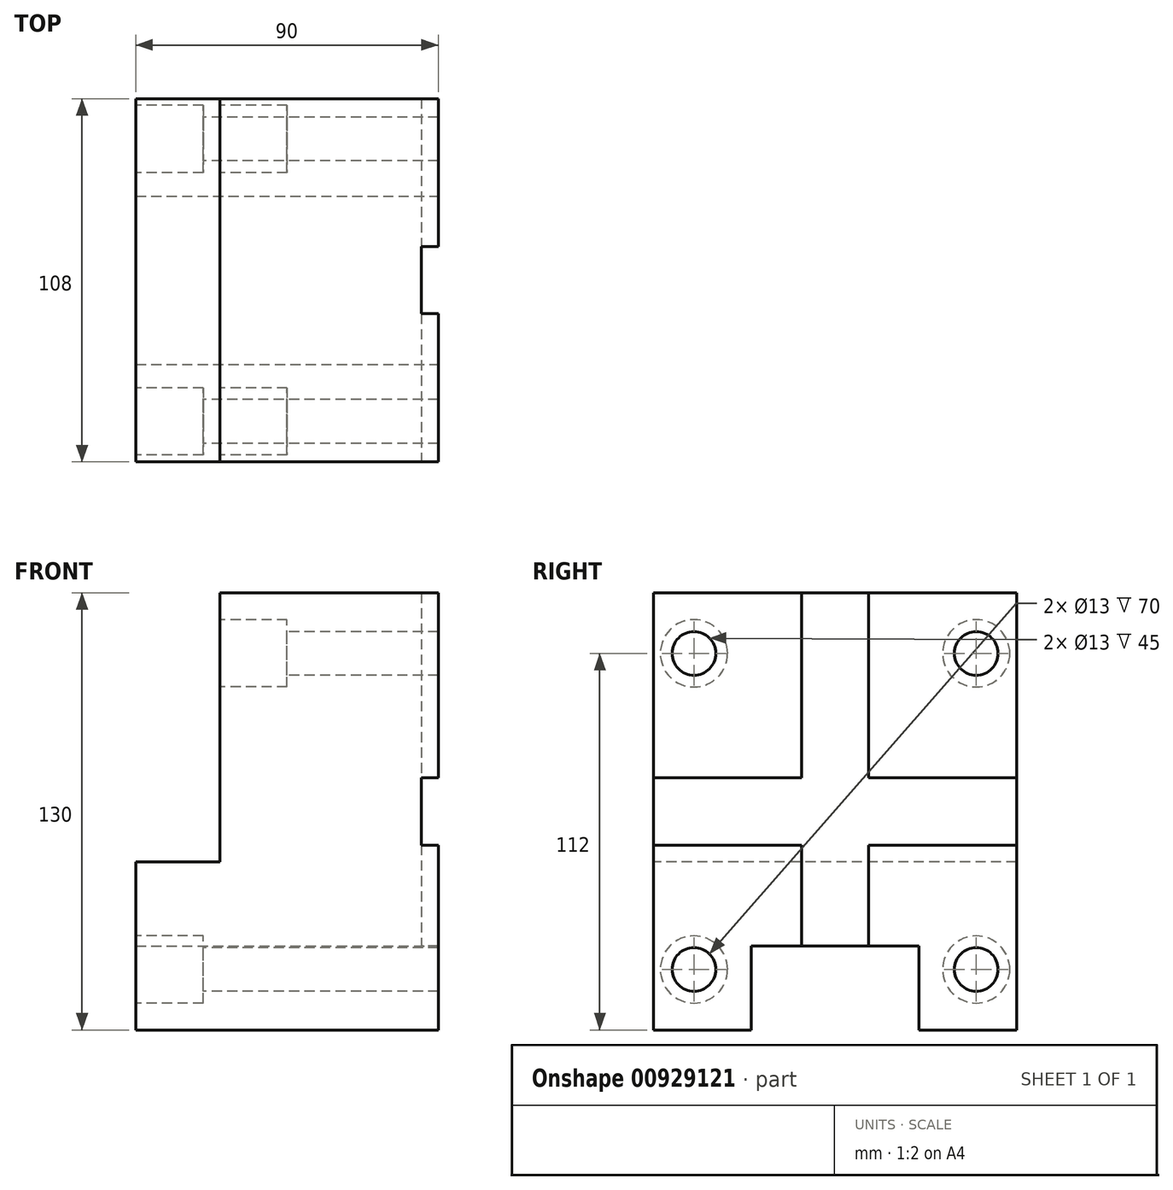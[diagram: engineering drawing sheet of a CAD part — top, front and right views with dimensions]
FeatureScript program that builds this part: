
annotation { "Feature Type Name" : "Feature", "Feature Type Description" : "" }
export const myFeature = defineFeature(function(context is Context, id is Id, definition is map)
    precondition{}
    {
        {
            var Q0;
            Q0=qCreatedBy(makeId("Right.planeOp"),FACE);
            var sketch = newSketch(context, id + "F0", { "sketchPlane" : qUnion([Q0])});
            skLineSegment(sketch, "E0.bottom", {"start": v(54, 65) * mm, "end": v(-54, 65) * mm});
            skLineSegment(sketch, "E0.top", {"start": v(54, -65) * mm, "end": v(-54, -65) * mm});
            skLineSegment(sketch, "E0.left", {"start": v(54, 65) * mm, "end": v(54, -65) * mm});
            skLineSegment(sketch, "E0.right", {"start": v(-54, 65) * mm, "end": v(-54, -65) * mm});
            skPoint(sketch, "E0.middle", {"position": v(0, 0) * mm});
            skSolve(sketch);
        }
        {
            var Q0;
            Q0 = qSketchRegion(id + "F0", true);
            extrude(context, id + "F1", {"entities" : qUnion([Q0]), "oppositeDirection" : true, "depth" : 90 * mm, "offsetDistance" : 25 * mm});
        }
        {
            var Q0;
            Q0=makeQuery(id+"F1.opExtrude","CAP_FACE",FACE,{"disambiguationData":[OSD([sQuery(id+"F0.wireOp",EDGE,"E0.bottom"),sQuery(id+"F0.wireOp",EDGE,"E0.top"),sQuery(id+"F0.wireOp",EDGE,"E0.left"),sQuery(id+"F0.wireOp",EDGE,"E0.right")])],"isStart":false});
            var sketch = newSketch(context, id + "F2", { "sketchPlane" : qUnion([Q0])});
            skCircle(sketch, "E1", {"center": v(-42, 47) * mm, "radius": 6.5 * mm});
            skCircle(sketch, "E2.MirrorC", {"center": v(42, 47) * mm, "radius": 6.5 * mm});
            skCircle(sketch, "E3.MirrorC", {"center": v(-42, -47) * mm, "radius": 6.5 * mm});
            skCircle(sketch, "E4.MirrorC", {"center": v(42, -47) * mm, "radius": 6.5 * mm});
            skSolve(sketch);
        }
        {
            var Q0;
            Q0 = qSketchRegion(id + "F2", true);
            extrude(context, id + "F3", {"entities" : qUnion([Q0]), "operationType" : NewBodyOperationType.REMOVE, "endBound" : BoundingType.THROUGH_ALL, "oppositeDirection" : true, "depth" : 25 * mm, "offsetDistance" : 25 * mm});
        }
        {
            var Q0;
            Q0=makeQuery(id+"F1.opExtrude","CAP_FACE",FACE,{"disambiguationData":[OSD([sQuery(id+"F0.wireOp",EDGE,"E0.bottom"),sQuery(id+"F0.wireOp",EDGE,"E0.top"),sQuery(id+"F0.wireOp",EDGE,"E0.left"),sQuery(id+"F0.wireOp",EDGE,"E0.right")])],"isStart":false});
            var sketch = newSketch(context, id + "F4", { "sketchPlane" : qUnion([Q0])});
            skLineSegment(sketch, "E5.bottom", {"start": v(54, -65) * mm, "end": v(-54, -65) * mm});
            skLineSegment(sketch, "E5.top", {"start": v(54, 15) * mm, "end": v(-54, 15) * mm});
            skLineSegment(sketch, "E5.left", {"start": v(54, -65) * mm, "end": v(54, 15) * mm});
            skLineSegment(sketch, "E5.right", {"start": v(-54, -65) * mm, "end": v(-54, 15) * mm});
            skSolve(sketch);
        }
        {
            var Q0;
            Q0 = qSketchRegion(id + "F4", true);
            extrude(context, id + "F5", {"entities" : qUnion([Q0]), "operationType" : NewBodyOperationType.REMOVE, "oppositeDirection" : true, "depth" : 25 * mm, "offsetDistance" : 25 * mm});
        }
        {
            var Q0;
            Q0=makeQuery(id+"F1.opExtrude","SWEPT_FACE",FACE,{"disambiguationData":[OSD([sQuery(id+"F0.wireOp",EDGE,"E0.bottom")])]});
            var sketch = newSketch(context, id + "F6", { "sketchPlane" : qUnion([Q0])});
            skLineSegment(sketch, "E6.bottom", {"start": v(-90, 25) * mm, "end": v(0, 25) * mm});
            skLineSegment(sketch, "E6.top", {"start": v(-90, -25) * mm, "end": v(0, -25) * mm});
            skLineSegment(sketch, "E6.left", {"start": v(-90, 25) * mm, "end": v(-90, -25) * mm});
            skLineSegment(sketch, "E6.right", {"start": v(0, 25) * mm, "end": v(0, -25) * mm});
            skPoint(sketch, "E6.middle", {"position": v(-45, 0) * mm});
            skSolve(sketch);
        }
        {
            var Q0;
            Q0 = qSketchRegion(id + "F6", true);
            extrude(context, id + "F7", {"entities" : qUnion([Q0]), "operationType" : NewBodyOperationType.REMOVE, "oppositeDirection" : true, "depth" : 25 * mm, "offsetDistance" : 25 * mm});
        }
        {
            var Q0;
            Q0=makeQuery(id+"F5.boolean.opBoolean","COPY",FACE,{"derivedFrom":makeQuery(id+"F5.opExtrude","CAP_FACE",FACE,{"disambiguationData":[OSD([sQuery(id+"F4.wireOp",EDGE,"E5.bottom"),sQuery(id+"F4.wireOp",EDGE,"E5.top"),sQuery(id+"F4.wireOp",EDGE,"E5.left"),sQuery(id+"F4.wireOp",EDGE,"E5.right")])],"isStart":false})});
            var sketch = newSketch(context, id + "F8", { "sketchPlane" : qUnion([Q0])});
            skCircle(sketch, "E7", {"center": v(42, -47) * mm, "radius": 10 * mm});
            skCircle(sketch, "E8", {"center": v(-42, -47) * mm, "radius": 10 * mm});
            skSolve(sketch);
        }
        {
            var Q0;
            Q0 = qSketchRegion(id + "F8", true);
            extrude(context, id + "F9", {"entities" : qUnion([Q0]), "operationType" : NewBodyOperationType.REMOVE, "oppositeDirection" : true, "depth" : 20 * mm, "offsetDistance" : 25 * mm});
        }
        {
            var Q0;
            Q0=makeQuery(id+"F1.opExtrude","CAP_FACE",FACE,{"disambiguationData":[OSD([sQuery(id+"F0.wireOp",EDGE,"E0.bottom"),sQuery(id+"F0.wireOp",EDGE,"E0.top"),sQuery(id+"F0.wireOp",EDGE,"E0.left"),sQuery(id+"F0.wireOp",EDGE,"E0.right")])],"isStart":false});
            var sketch = newSketch(context, id + "F10", { "sketchPlane" : qUnion([Q0])});
            skCircle(sketch, "E9", {"center": v(42, 47) * mm, "radius": 10 * mm});
            skCircle(sketch, "E10", {"center": v(-42, 47) * mm, "radius": 10 * mm});
            skSolve(sketch);
        }
        {
            var Q0;
            Q0 = qSketchRegion(id + "F10", true);
            extrude(context, id + "F11", {"entities" : qUnion([Q0]), "operationType" : NewBodyOperationType.REMOVE, "oppositeDirection" : true, "depth" : 20 * mm, "offsetDistance" : 25 * mm});
        }
        {
            var Q0;
            Q0=makeQuery(id+"F1.opExtrude","CAP_FACE",FACE,{"disambiguationData":[OSD([sQuery(id+"F0.wireOp",EDGE,"E0.bottom"),sQuery(id+"F0.wireOp",EDGE,"E0.top"),sQuery(id+"F0.wireOp",EDGE,"E0.left"),sQuery(id+"F0.wireOp",EDGE,"E0.right")])],"isStart":true});
            var sketch = newSketch(context, id + "F12", { "sketchPlane" : qUnion([Q0])});
            skLineSegment(sketch, "E11.bottom", {"start": v(-10, -65) * mm, "end": v(10, -65) * mm});
            skLineSegment(sketch, "E11.top", {"start": v(-10, 65) * mm, "end": v(10, 65) * mm});
            skLineSegment(sketch, "E11.left", {"start": v(-10, -65) * mm, "end": v(-10, 65) * mm});
            skLineSegment(sketch, "E11.right", {"start": v(10, -65) * mm, "end": v(10, 65) * mm});
            skPoint(sketch, "E11.middle", {"position": v(0, 0) * mm});
            skLineSegment(sketch, "E12.bottom", {"start": v(-54, 10) * mm, "end": v(54, 10) * mm});
            skLineSegment(sketch, "E12.top", {"start": v(-54, -10) * mm, "end": v(54, -10) * mm});
            skLineSegment(sketch, "E12.left", {"start": v(-54, 10) * mm, "end": v(-54, -10) * mm});
            skLineSegment(sketch, "E12.right", {"start": v(54, 10) * mm, "end": v(54, -10) * mm});
            skSolve(sketch);
        }
        {
            var Q0;
            Q0 = qSketchRegion(id + "F12", true);
            extrude(context, id + "F13", {"entities" : qUnion([Q0]), "operationType" : NewBodyOperationType.REMOVE, "oppositeDirection" : true, "depth" : 5 * mm, "offsetDistance" : 25 * mm});
        }
        {
            var Q0;
            Q0=qCreatedBy(makeId("Top.planeOp"),FACE);
            var sketch = newSketch(context, id + "F14", { "sketchPlane" : qUnion([Q0])});
            skLineSegment(sketch, "E13", {"start": v(0, 0) * mm, "end": v(85.6, 0) * mm, "construction": true});
            skSolve(sketch);
        }
        {
            var Q0;
            Q0=makeQuery(id+"F1.opExtrude","SWEPT_BODY",BODY,{"disambiguationData":[OSD([sQuery(id+"F0.wireOp",EDGE,"E0.bottom"),sQuery(id+"F0.wireOp",EDGE,"E0.top"),sQuery(id+"F0.wireOp",EDGE,"E0.left"),sQuery(id+"F0.wireOp",EDGE,"E0.right")])]});
            var Q1;
            Q1=sQuery(id+"F14.wireOp",EDGE,"E13");
            transform(context, id + "F15", {"entities" : qUnion([Q0]), "transformType" : TransformType.ROTATION, "transformAxis" : qUnion([Q1]), "angle" : 180 * degree, "makeCopy" : false});
        }
    });
